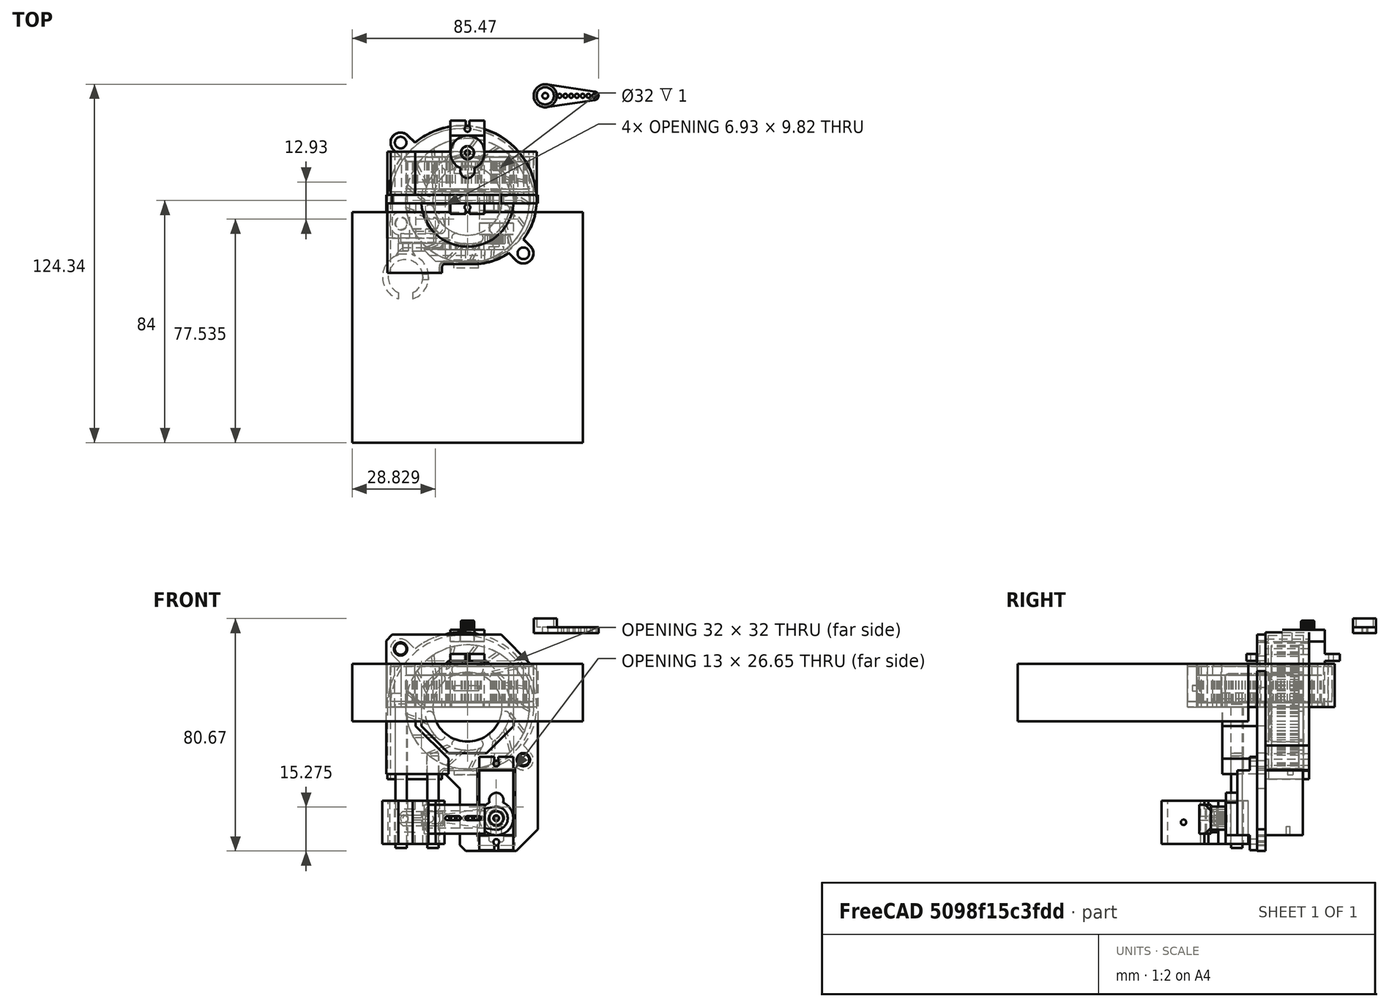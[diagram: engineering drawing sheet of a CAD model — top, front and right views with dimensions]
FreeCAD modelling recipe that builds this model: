
FCSTD DOCUMENT  (FreeCAD 0.17R13522 (Git))
Label: plotter_pen12mm
License: All rights reserved
LicenseURL: http://en.wikipedia.org/wiki/All_rights_reserved
objects: Part::Box×15, Part::Cylinder×15, App::DocumentObjectGroup×11, Part::Cut×11, PartDesign::ShapeBinder×7, Part::Fuse×7, Sketcher::SketchObject×7, Part::MultiFuse×7, Part::Feature×6, Part::Chamfer×6, PartDesign::Point×5, Part::Part2DObjectPython×4, PartDesign::Pocket×4, Mesh::Feature×3, PartDesign::Pad×3, Part::Fillet×2, PartDesign::Body×2, Part::Compound×1, Spreadsheet::Sheet×1, Part::FeaturePython×1, +1 more types
note: 111 computed .brp shape members not serialized (recipe doc carries the construction recipe); baked Part::Feature solids carry a one-line shape summary decoded from their .brp

FEATURE [Part::Feature] Part__Feature  label="TFD-B5015 TITAN"
  Placement = pos=(0,0,7.5) rot=(0,0,1;0rad)
  shape: bbox 51.8 x 51.1 x 15 mm, 65 faces (baked)
FEATURE [Part::Feature] Part__Feature001  label="TFD-B5015 TITAN001"
  shape: bbox 43 x 43 x 11.5 mm, 91 faces (baked)
FEATURE [Part::Part2DObjectPython] Line  # Draft 2D object (typed FeaturePython)
  ChamferSize = 0
  Closed = false
  End = (0,0,10.5)
  FilletRadius = 0
  MakeFace = false
  MapMode = 5
  Points = (2) [(-2.07596,14.8557,11),(0,0,10.5)]
  Start = (-2.07596,14.8557,11)
  Support = -> [Part__Feature001]
FEATURE [Part::Part2DObjectPython] Line001  # Draft 2D object (typed FeaturePython)
  ChamferSize = 0
  Closed = false
  End = (4.6539,11.0608,10.5)
  FilletRadius = 0
  MakeFace = false
  MapMode = 5
  Points = (2) [(0,0,10.5),(4.6539,11.0608,10.5)]
  Start = (0,0,10.5)
  Support = -> [Part__Feature001]
FEATURE [Part::Fillet] Fillet
  Edges = 1 edges r=1: [Edge57]
FEATURE [App::DocumentObjectGroup] Group  label="Inner-part-src"
  Group = -> [Fillet]
FEATURE [Part::Feature] Fillet001  label="Inner-part-final"
  shape: bbox 43 x 43 x 11.5 mm, 153 faces (baked)
FEATURE [Part::Part2DObjectPython] Line002  # Draft 2D object (typed FeaturePython)
  ChamferSize = 0
  Closed = false
  End = (19.4,-18.3,15)
  FilletRadius = 0
  MakeFace = false
  MapMode = 5
  Points = (2) [(0,0,15),(19.4,-18.3,15)]
  Start = (0,0,15)
  Support = -> [Part__Feature]
FEATURE [Part::Part2DObjectPython] Line003  # Draft 2D object (typed FeaturePython)
  ChamferSize = 0
  Closed = false
  End = (-23.2,20.1,15)
  FilletRadius = 0
  MakeFace = false
  MapMode = 5
  Points = (2) [(0,0,15),(-23.2,20.1,15)]
  Start = (0,0,15)
  Support = -> [Part__Feature]
FEATURE [App::DocumentObjectGroup] Construction
  Group = -> [Line,Line001,Line002,Line003]
FEATURE [Part::Cut] Cut  label="cover-1"
  Refine = true
FEATURE [App::DocumentObjectGroup] Group001  label="cover-src"
  Group = -> [Cut]
FEATURE [Part::Feature] Pad005001  label="cover-final"
  Placement = pos=(0,0,-2) rot=(0,0,1;0rad)
  shape: bbox 51.8 x 51 x 15 mm, 33 faces (baked)
FEATURE [Part::Compound] Compound  label="Blower-50x50-final"
  Links = -> [Fillet001,Pad005001]
  Placement = pos=(0,15,0) rot=(1,0,0;1.5708rad)
FEATURE [App::DocumentObjectGroup] Group002  label="Blower"
  Group = -> [Part__Feature,Part__Feature001,Construction,Group,Group001,Compound]
FEATURE [Mesh::Feature] original
FEATURE [Part::Box] Box  label="Cubo"
  AttacherType = Attacher::AttachEngine3D
  Height = 20
  Length = 80
  Placement = pos=(-40,-84,-5) rot=(0,0,1;0rad)
  Width = 80
FEATURE [Mesh::Feature] difference
FEATURE [Mesh::Feature] union
  Placement = pos=(-23,50.7,-49.11) rot=(0,0,1;3.14159rad)
FEATURE [App::DocumentObjectGroup] Group003  label="Fan duct"
  Group = -> [original,Box,difference,union]
FEATURE [PartDesign::ShapeBinder] CopyCompound
  Placement = pos=(0,2,0) rot=(1,0,0;1.5708rad)
FEATURE [PartDesign::Point] DatumPoint  label="DatumPoint_MainScrew1"
  AttacherType = Attacher::AttachEnginePoint
  MapMode = 36
  Placement = pos=(-23.2,2,20.1) rot=(1,0,0;3.14159rad)
  Support = -> [CopyCompound]
FEATURE [PartDesign::ShapeBinder] CopyCompound001
  Placement = pos=(0,2,0) rot=(1,0,0;1.5708rad)
FEATURE [PartDesign::Point] DatumPoint001  label="DatumPoint_MainScrew2"
  AttacherType = Attacher::AttachEnginePoint
  MapMode = 36
  Placement = pos=(19.4,2,-18.3) rot=(1,0,0;3.14159rad)
  Support = -> [CopyCompound001]
FEATURE [Spreadsheet::Sheet] Spreadsheet
  cells = A2=Fan hole diameter; B2(fanHoleDiam)=32; A3=Fan support thickness; B3(FanSuppThick)=3; A4=Fan support width; B4(FanSuppWidth)=10; A5=Shaft thickness; B5(shaftThick)=4; A6=Left Shaft length; B6(shaftLength)=50; A7=Right shaft length; B7(shaftLengthRight)=33; A9=Shaft Axis X position; B9(AxisX)==-Spreadsheet.FanSuppWidth - 13; A10=Shaft Axis Y position; B10(AxisY)=-8; A12=Shaft Axis tolerance; B12(AxisTolerance)=0.20000000000000001; A13=Shaft Axis separation; B13(AxisSeparation)=11; A15=Servo Connecting Rod Flexible Part Thickness; B15(FlexThickness)=0.80000000000000004; A18=Agrandar el prisionero de M2 a M3; A19=Tornillos soporte principal M3; A20=Modificar parte flexible al doble de tamaño
FEATURE [Part::Box] Box001  label="Cubo001"
  AttacherType = Attacher::AttachEngine3D
  Height = 22.7
  Length = 11.8
  Width = 22.5
FEATURE [Part::Box] Box002  label="Cubo002"
  AttacherType = Attacher::AttachEngine3D
  Height = 2.5
  Length = 11.8
  Placement = pos=(0,-4.7,15.9) rot=(0,0,1;0rad)
  Width = 32.4
FEATURE [Part::Fuse] Fusion  label="Square_body"
  Base = -> Box001
  Refine = true
  Tool = -> Box002
FEATURE [Part::Cylinder] Cylinder  label="Cilindro"
  Angle = 360
  AttacherType = Attacher::AttachEngine3D
  Height = 4
  Placement = pos=(5.9,16.6,22.7) rot=(0,0,1;0rad)
  Radius = 5.9
FEATURE [Part::Cylinder] Cylinder001  label="Cilindro001"
  Angle = 360
  AttacherType = Attacher::AttachEngine3D
  Height = 4
  Placement = pos=(5.9,10.3,22.7) rot=(0,0,1;0rad)
  Radius = 2.5
FEATURE [Part::Fuse] Fusion001
  Base = -> Cylinder
  Refine = true
  Tool = -> Cylinder001
FEATURE [Part::Fuse] Fusion003
  Base = -> Fusion
  Refine = true
  Tool = -> Fusion001
FEATURE [Part::Cylinder] Cylinder003  label="Taladro"
  Angle = 360
  AttacherType = Attacher::AttachEngine3D
  Height = 10
  Placement = pos=(5.9,-2.35,11) rot=(0,0,1;0rad)
  Radius = 1
FEATURE [Part::Cylinder] Cylinder004  label="Taladro2"
  Angle = 360
  AttacherType = Attacher::AttachEngine3D
  Height = 10
  Placement = pos=(5.9,24.85,11) rot=(0,0,1;0rad)
  Radius = 1
FEATURE [Part::Fuse] Fusion004  label="Taladros"
  Base = -> Cylinder003
  Refine = true
  Tool = -> Cylinder004
FEATURE [Part::Box] Box003  label="Cubo003"
  AttacherType = Attacher::AttachEngine3D
  Height = 10
  Length = 1.3
  Placement = pos=(5.25,-6,12) rot=(0,0,1;0rad)
  Width = 3.3
FEATURE [Part::Box] Box004  label="Cubo004"
  AttacherType = Attacher::AttachEngine3D
  Height = 10
  Length = 1.3
  Placement = pos=(5.25,25,12) rot=(0,0,1;0rad)
  Width = 3.3
FEATURE [Part::Fuse] Fusion005  label="Rebajes"
  Base = -> Box003
  Refine = true
  Tool = -> Box004
FEATURE [Part::Fuse] Fusion006  label="Taladros001"
  Base = -> Fusion004
  Refine = true
  Tool = -> Fusion005
FEATURE [Part::Cut] Cut001  label="Cuerpo_con_taladros"
  Base = -> Fusion003
  Placement = pos=(-5.9,0,0) rot=(0,0,1;0rad)
  Refine = true
  Tool = -> Fusion006
FEATURE [Part::Cylinder] Cylinder006  label="Cilindro002"
  Angle = 360
  AttacherType = Attacher::AttachEngine3D
  Height = 3
  Placement = pos=(2.51021,16.5511,26.9) rot=(0,0,1;0rad)
  Radius = 0.35
FEATURE [Part::FeaturePython] Array  # Draft array (typed FeaturePython)
  Angle = 360
  ArrayType = 1
  Axis = (0,0,1)
  Base = -> Cylinder006
  Center = (0,16.6,0)
  Fuse = false
  IntervalAxis = (0,0,0)
  IntervalX = (1,0,0)
  IntervalY = (0,1,0)
  IntervalZ = (0,0,0)
  NumberPolar = 20
  NumberX = 2
  NumberY = 2
  NumberZ = 1
FEATURE [Part::Cylinder] Cylinder002  label="Cilindro_interior"
  Angle = 360
  AttacherType = Attacher::AttachEngine3D
  Height = 3.2
  Placement = pos=(0,16.6,26.7) rot=(0,0,1;0rad)
  Radius = 2.3
FEATURE [Part::Cylinder] Cylinder005  label="Cilindro_exterior"
  Angle = 360
  AttacherType = Attacher::AttachEngine3D
  Height = 3.2
  Placement = pos=(0,16.6,26.7) rot=(0,0,1;0rad)
  Radius = 0.85
FEATURE [Part::Cut] Cut002  label="Cilindro_vaciado"
  Base = -> Cylinder002
  Refine = true
  Tool = -> Cylinder005
FEATURE [Part::Fillet] Fillet002
  Base = -> Cut002
  Edges = 1 edges r=0.3: [Edge1]
FEATURE [Part::Cut] Cut003  label="Eje_engranaje"
  Base = -> Fillet002
  Refine = true
  Tool = -> Array
FEATURE [Part::Feature] Fusion007001  label="Servo-sg90-final"
  Placement = pos=(10,14.9,-22) rot=(0,0.707107,-0.707107;3.14159rad)
  shape: bbox 11.8 x 29.9 x 32.4 mm, 77 faces (baked)
  expr: Placement.Base.y = 17.899999999999999 - Spreadsheet.FanSuppThick
FEATURE [App::DocumentObjectGroup] Grupo003  label="Servo"
  Group = -> [Cut001,Cut003,Fusion007001]
FEATURE [Part::Fuse] Fusion008
  Placement = pos=(26.9697,36.3362,25.6722) rot=(0,0,1;0rad)
  Refine = true
FEATURE [App::DocumentObjectGroup] Grupo001  label="1-arm-horn"
  Group = -> [Fusion008]
FEATURE [Part::Feature] Pocket002001  label="Final-1-arm-horn"
  Placement = pos=(9.96971,-16.96,-38.6278) rot=(0,0.707107,0.707107;3.14159rad)
  shape: bbox 22.5 x 5 x 8 mm, 19 faces (baked)
  expr: Placement.Base.y = -13.960000000000001 - Spreadsheet.FanSuppThick
FEATURE [App::DocumentObjectGroup] Group004  label="ServoArm"
  Group = -> [Grupo001,Pocket002001]
FEATURE [PartDesign::ShapeBinder] CopyFusion007001
FEATURE [PartDesign::Point] DatumPoint002  label="DatumPoint_ServoHeight"
  AttacherType = Attacher::AttachEnginePoint
  MapMode = 37
  Placement = pos=(15.9,-8.8,-22) rot=(0,0,1;0rad)
  Support = -> [CopyFusion007001]
FEATURE [PartDesign::ShapeBinder] CopyFusion007001001
  Placement = pos=(15.9,13.9,-22) rot=(0,0.707107,-0.707107;3.14159rad)
FEATURE [PartDesign::Point] DatumPoint003  label="DatumPoint_ServoScrew1"
  AttacherType = Attacher::AttachEnginePoint
  MapMode = 36
  Placement = pos=(10,-4.5,-19.65) rot=(0,0,1;3.14159rad)
  Support = -> [CopyFusion007001001]
FEATURE [PartDesign::ShapeBinder] CopyFusion007001002
  Placement = pos=(15.9,13.9,-22) rot=(0,0.707107,-0.707107;3.14159rad)
FEATURE [PartDesign::Point] DatumPoint004  label="DatumPoint_ServoScrew2"
  AttacherType = Attacher::AttachEnginePoint
  MapMode = 36
  Placement = pos=(10,-4.5,-46.85) rot=(0.908295,0,-0.41833;3.14159rad)
  Support = -> [CopyFusion007001002]
FEATURE [Sketcher::SketchObject] Sketch  label="Sketch_SupportBase"
  ExternalGeometry = -> [DatumPoint,DatumPoint001,DatumPoint002,DatumPoint003,DatumPoint004]
  MapMode = 5
  Placement = pos=(0,0,0) rot=(1,0,0;1.5708rad)
  Support = -> [XZ_Plane]
  expr: Constraints[3] = 0.5 * Spreadsheet.FanSuppWidth
  expr: Constraints[34] = Spreadsheet.fanHoleDiam * 0.5
  expr: Constraints[4] = 0.5 * Spreadsheet.FanSuppWidth
  expr: Constraints[71] = 0.5 * Spreadsheet.FanSuppWidth
  expr: Constraints[72] = 0.5 * Spreadsheet.FanSuppWidth
  sketch-geometry (29):
    g0: LineSegment StartX=-26.0787 StartY=25.1 StartZ=0 EndX=11.6721 EndY=25.1 EndZ=0
    g1: LineSegment StartX=24.4 StartY=12.3721 StartZ=0 EndX=24.4 EndY=-23.3 EndZ=0
    g2: LineSegment StartX=-28.2 StartY=-23.3 StartZ=0 EndX=-28.2 EndY=22.9787 EndZ=0
    g3: Circle CenterX=-23.2 CenterY=20.1 CenterZ=0 NormalX=0 NormalY=0 NormalZ=1 AngleXU=0 Radius=2.3
    g4: Circle CenterX=19.4 CenterY=-18.3 CenterZ=0 NormalX=0 NormalY=0 NormalZ=1 AngleXU=0 Radius=2.3
    g5: LineSegment StartX=16 StartY=6.62742 StartZ=0 EndX=6.62742 EndY=16 EndZ=0
    g6: LineSegment StartX=6.62742 StartY=16 StartZ=0 EndX=-6.62742 EndY=16 EndZ=0
    g7: LineSegment StartX=-6.62742 StartY=16 StartZ=0 EndX=-16 EndY=6.62742 EndZ=0
    g8: LineSegment StartX=-16 StartY=6.62742 StartZ=0 EndX=-16 EndY=-6.62742 EndZ=0
    g9: LineSegment StartX=-16 StartY=-6.62742 StartZ=0 EndX=-6.62742 EndY=-16 EndZ=0
    g10: LineSegment StartX=-6.62742 StartY=-16 StartZ=0 EndX=6.62742 EndY=-16 EndZ=0
    g11: LineSegment StartX=6.62742 StartY=-16 StartZ=0 EndX=16 EndY=-6.62742 EndZ=0
    g12: LineSegment StartX=16 StartY=-6.62742 StartZ=0 EndX=16 EndY=6.62742 EndZ=0
    g13: Circle [constr] CenterX=0 CenterY=0 CenterZ=0 NormalX=0 NormalY=0 NormalZ=1 AngleXU=0 Radius=17.3183
    g14: LineSegment StartX=16.9 StartY=-50 StartZ=0 EndX=-0.551549 EndY=-50 EndZ=0
    g15: LineSegment StartX=-7.74282 StartY=-23.3 StartZ=0 EndX=-28.2 EndY=-23.3 EndZ=0
    g16: Circle CenterX=10.0164 CenterY=-19.6473 CenterZ=0 NormalX=0 NormalY=0 NormalZ=1 AngleXU=0 Radius=1
    g17: LineSegment StartX=16.9 StartY=-50 StartZ=0 EndX=24.4 EndY=-42.5 EndZ=0
    g18: LineSegment StartX=24.4 StartY=-23.3 StartZ=0 EndX=24.4 EndY=-42.5 EndZ=0
    g19: LineSegment StartX=-2.67287 StartY=-28.37 StartZ=0 EndX=-2.67287 EndY=-47.8787 EndZ=0
    g20: LineSegment StartX=-2.67287 StartY=-47.8787 StartZ=0 EndX=-0.551549 EndY=-50 EndZ=0
    g21: LineSegment StartX=3.5 StartY=-21.4 StartZ=0 EndX=16.5 EndY=-21.4 EndZ=0
    g22: LineSegment StartX=16.5 StartY=-21.4 StartZ=0 EndX=16.5 EndY=-45 EndZ=0
    g23: LineSegment StartX=16.5 StartY=-45 StartZ=0 EndX=3.5 EndY=-45 EndZ=0
    g24: LineSegment StartX=3.5 StartY=-45 StartZ=0 EndX=3.5 EndY=-21.4 EndZ=0
    g25: Circle CenterX=10 CenterY=-46.85 CenterZ=0 NormalX=0 NormalY=0 NormalZ=1 AngleXU=0 Radius=1.2
    g26: LineSegment StartX=11.6721 StartY=25.1 StartZ=0 EndX=24.4 EndY=12.3721 EndZ=0
    g27: LineSegment StartX=-26.0787 StartY=25.1 StartZ=0 EndX=-28.2 EndY=22.9787 EndZ=0
    g28: LineSegment StartX=-2.67287 StartY=-28.37 StartZ=0 EndX=-7.74282 EndY=-23.3 EndZ=0
  constraints (75):
    c: Horizontal(g0)
    c: Vertical(g1)
    c: Vertical(g2)
    c: DistanceY(g1,g-4) = 5
    c: DistanceX(g-4,g1) = 5
    c: Coincident(g3,g-3)
    c: Radius(g3) = 2.3
    c: Coincident(g4,g-4)
    c: Radius(g4) = 2.3
    c: Coincident(g5,g6)
    c: Coincident(g6,g7)
    c: Coincident(g7,g8)
    c: Coincident(g8,g9)
    c: Coincident(g9,g10)
    c: Coincident(g10,g11)
    c: Coincident(g11,g12)
    c: Coincident(g12,g5)
    c: Equal(g5, g6-g12) x7
    c: PointOnObject(g5,g13)
    c: PointOnObject(g6,g13)
    c: PointOnObject(g7,g13)
    c: PointOnObject(g8,g13)
    c: PointOnObject(g9,g13)
    c: PointOnObject(g10,g13)
    c: PointOnObject(g11,g13)
    c: PointOnObject(g12,g13)
    c: Coincident(g13,g-1)
    c: Horizontal(g6)
    c: DistanceY(g-1,g5) = 16
    c: DistanceY(g-5,g14) = -28
    c: Horizontal(g14)
    c: DistanceX(g-5,g14) = 1
    c: Coincident(g15,g2)
    c: Radius(g16) = 1.2
    c: Block(g16)
    c: Coincident(g17,g14)
    c: Coincident(g18,g17)
    c: Vertical(g18)
    c: Angle(g18,g17) = 2.35619
    c: Vertical(g19)
    c: Coincident(g19,g20)
    c: Coincident(g20,g14)
    c: Angle(g20,g19) = 2.35619
    c: Coincident(g21,g22)
    c: Coincident(g22,g23)
    c: Coincident(g23,g24)
    c: Coincident(g24,g21)
    c: Horizontal(g21)
    c: Horizontal(g23)
    c: Vertical(g22)
    c: Vertical(g24)
    c: DistanceX(g-5,g21) = 0.6
    c: DistanceY(g-5,g21) = 0.6
    c: DistanceX(g23,g21) = 13
    c: DistanceY(g23,g21) = 23.6
    c: Horizontal(g15)
    c: PointOnObject(g1,g15)
    c: Coincident(g25,g-7)
    c: Radius(g25) = 1.2
    c: Coincident(g0,g26)
    c: Coincident(g26,g1)
    c: Angle(g0,g26) = 2.35619
    c: Distance(g26) = 18
    c: Coincident(g2,g27)
    c: Coincident(g0,g27)
    c: DistanceX(g2,g3) = 5
    c: DistanceY(g3,g0) = 5
    c: Distance(g27) = 3
    c: Angle(g27,g0) = 2.35619
    c: Coincident(g18,g1)
    c: Distance(g20) = 3
    c: Coincident(g15,g28)
    c: Coincident(g28,g19)
    c: Angle(g15,g28) = 2.35619
    c: Distance(g28) = 7.17
FEATURE [PartDesign::Pad] Pad
  Length = 3
  Length2 = 100
  Placement = pos=(0,0,0) rot=(1,0,0;1.5708rad)
  Profile = -> Sketch
  Type = 0
  expr: Length = Spreadsheet.FanSuppThick
FEATURE [Sketcher::SketchObject] Sketch001  label="Sketch_AxisSupport"
  ExternalGeometry = -> [Pad]
  MapMode = 5
  Placement = pos=(0,-3,0) rot=(1,0,0;1.5708rad)
  Support = -> [Pad]
  sketch-geometry (8):
    g0: LineSegment StartX=-26.0787 StartY=4.82132 StartZ=0 EndX=-20.1213 EndY=4.82132 EndZ=0
    g1: LineSegment StartX=-18 StartY=2.7 StartZ=0 EndX=-20.1213 EndY=4.82132 EndZ=0
    g2: LineSegment StartX=-26.0787 StartY=4.82132 StartZ=0 EndX=-28.2 EndY=2.7 EndZ=0
    g3: LineSegment StartX=-18 StartY=2.7 StartZ=0 EndX=-18 EndY=-6.62742 EndZ=0
    g4: LineSegment StartX=-18 StartY=-6.62742 StartZ=0 EndX=-6.62742 EndY=-18 EndZ=0
    g5: LineSegment StartX=-6.62742 StartY=-18 StartZ=0 EndX=-6.62742 EndY=-23.3 EndZ=0
    g6: LineSegment StartX=-6.62742 StartY=-23.3 StartZ=0 EndX=-28.2 EndY=-23.3 EndZ=0
    g7: LineSegment StartX=-28.2 StartY=-23.3 StartZ=0 EndX=-28.2 EndY=2.7 EndZ=0
  constraints (23):
    c: Horizontal(g0)
    c: Coincident(g1,g0)
    c: Coincident(g0,g2)
    c: Angle(g2,g0) = 2.35619
    c: Angle(g0,g1) = 2.35619
    c: Equal(g1,g2)
    c: Distance(g1) = 3
    c: Vertical(g3)
    c: Coincident(g3,g4)
    c: Coincident(g4,g5)
    c: Vertical(g5)
    c: Coincident(g5,g6)
    c: Coincident(g6,g-3)
    c: Horizontal(g6)
    c: Coincident(g6,g7)
    c: Vertical(g7)
    c: Coincident(g7,g2)
    c: Coincident(g3,g1)
    c: PointOnObject(g-4,g5)
    c: DistanceY(g4,g-4) = 2
    c: DistanceX(g3,g-4) = 2
    c: Angle(g4,g3) = 2.35619
    c: DistanceY(g6,g2) = 26
FEATURE [Part::Cylinder] Cylinder007  label="ShaftLeft"
  Angle = 360
  AttacherType = Attacher::AttachEngine3D
  Height = 50
  Placement = pos=(-23,-8,-49) rot=(0,0,1;0rad)
  Radius = 2
  expr: Placement.Base.y = Spreadsheet.AxisY
  expr: Placement.Base.x = Spreadsheet.AxisX
  expr: Height = Spreadsheet.shaftLength
  expr: Radius = Spreadsheet.shaftThick * 0.5
FEATURE [PartDesign::Pad] Pad005002
  BaseFeature = -> Pad
  Length = 12
  Length2 = 100
  Placement = pos=(0,0,0) rot=(1,0,0;1.5708rad)
  Profile = -> Sketch001
  Type = 0
FEATURE [Part::Cylinder] Cylinder008  label="ShaftRight"
  Angle = 360
  AttacherType = Attacher::AttachEngine3D
  Height = 33
  Placement = pos=(-12,-8,-49) rot=(0,0,1;0rad)
  Radius = 2
  expr: Placement.Base.y = Spreadsheet.AxisY
  expr: Placement.Base.x = Spreadsheet.AxisX + Spreadsheet.AxisSeparation
  expr: Height = Spreadsheet.shaftLengthRight
  expr: Radius = Spreadsheet.shaftThick * 0.5
FEATURE [Sketcher::SketchObject] Sketch002  label="Sketch_AxisLeftHole"
  AttachmentOffset = pos=(24,0,-28.2) rot=(0,1,0;1.5708rad)
  MapMode = 5
  Placement = pos=(0,2e-12,-24) rot=(1,0,0;3.14159rad)
  Support = -> [Pad005002]
  expr: Constraints[4] = 2.1499999999999999
  expr: Constraints[3] = Spreadsheet.AxisSeparation
  expr: Constraints[1] = -Spreadsheet.AxisY + 2
  expr: Constraints[0] = -Spreadsheet.AxisX
  sketch-geometry (2):
    g0: Circle CenterX=-23 CenterY=10 CenterZ=0 NormalX=0 NormalY=0 NormalZ=1 AngleXU=0 Radius=2.15
    g1: Circle [constr] CenterX=-12 CenterY=10 CenterZ=0 NormalX=0 NormalY=0 NormalZ=1 AngleXU=0 Radius=2.15
  constraints (6):
    c: DistanceX(g0,g-1) = 23
    c: DistanceY(g-1,g0) = 10
    c: DistanceY(g1,g0) = 0
    c: DistanceX(g0,g1) = 11
    c: Radius(g1) = 2.15
    c: Radius(g0) = 2.15
FEATURE [Sketcher::SketchObject] Sketch003  label="Sketch_AxisRightHole"
  AttachmentOffset = pos=(24,0,-28.2) rot=(0,1,0;1.5708rad)
  MapMode = 5
  Placement = pos=(0,2e-12,-24) rot=(1,0,0;3.14159rad)
  Support = -> [Pad005002]
  expr: Constraints[4] = 2.1499999999999999
  expr: Constraints[3] = Spreadsheet.AxisSeparation
  expr: Constraints[1] = -Spreadsheet.AxisY + 2
  expr: Constraints[0] = -Spreadsheet.AxisX
  sketch-geometry (2):
    g0: Circle [constr] CenterX=-23 CenterY=10 CenterZ=0 NormalX=0 NormalY=0 NormalZ=1 AngleXU=0 Radius=2.15
    g1: Circle CenterX=-12 CenterY=10 CenterZ=0 NormalX=0 NormalY=0 NormalZ=1 AngleXU=0 Radius=2.15
  constraints (6):
    c: DistanceX(g0,g-1) = 23
    c: DistanceY(g-1,g0) = 10
    c: DistanceY(g1,g0) = 0
    c: DistanceX(g0,g1) = 11
    c: Radius(g1) = 2.15
    c: Radius(g0) = 2.15
FEATURE [PartDesign::Pocket] Pocket
  BaseFeature = -> Pad005002
  Length = 24
  Length2 = 100
  Placement = pos=(0,0,0) rot=(1,0,0;1.5708rad)
  Profile = -> Sketch002
  Type = 0
FEATURE [PartDesign::Pocket] Pocket002002
  BaseFeature = -> Pocket
  Length = 7
  Length2 = 100
  Placement = pos=(0,0,0) rot=(1,0,0;1.5708rad)
  Profile = -> Sketch003
  Type = 0
FEATURE [Sketcher::SketchObject] Sketch004  label="Sketch_ServoCableHole"
  ExternalGeometry = -> [Pocket002002]
  MapMode = 5
  Placement = pos=(0,-3,0) rot=(1,0,0;1.5708rad)
  Support = -> [Pocket002002]
  sketch-geometry (7):
    g0: LineSegment StartX=12.5 StartY=-43.35 StartZ=0 EndX=7.5 EndY=-43.35 EndZ=0
    g1: LineSegment StartX=7.5 StartY=-43.35 StartZ=0 EndX=7.5 EndY=-46.35 EndZ=0
    g2: LineSegment StartX=7.5 StartY=-46.35 StartZ=0 EndX=8 EndY=-46.85 EndZ=0
    g3: LineSegment StartX=12 StartY=-46.85 StartZ=0 EndX=12.5 EndY=-46.35 EndZ=0
    g4: LineSegment StartX=12.5 StartY=-46.35 StartZ=0 EndX=12.5 EndY=-43.35 EndZ=0
    g5: LineSegment StartX=8 StartY=-46.85 StartZ=0 EndX=10 EndY=-46.85 EndZ=0
    g6: LineSegment StartX=10 StartY=-46.85 StartZ=0 EndX=12 EndY=-46.85 EndZ=0
  constraints (20):
    c: Horizontal(g0)
    c: Coincident(g0,g1)
    c: Vertical(g1)
    c: Coincident(g1,g2)
    c: Coincident(g3,g4)
    c: Coincident(g4,g0)
    c: Vertical(g4)
    c: Equal(g2,g3)
    c: Coincident(g5,g2)
    c: Coincident(g5,g-3)
    c: Horizontal(g5)
    c: Coincident(g6,g5)
    c: Coincident(g6,g3)
    c: Equal(g6,g5)
    c: Horizontal(g6)
    c: Equal(g4,g1)
    c: DistanceX(g0,g0) = 5
    c: DistanceX(g6,g6) = 2
    c: Angle(g3,g6) = 2.35619
    c: DistanceY(g4,g4) = 3
FEATURE [PartDesign::Pocket] Pocket002003
  BaseFeature = -> Pocket002002
  Length = 5
  Length2 = 100
  Placement = pos=(0,0,0) rot=(1,0,0;1.5708rad)
  Profile = -> Sketch004
  Type = 1
FEATURE [PartDesign::Body] Body  label="Part 1 - MainSupportPart"
  Group = -> [Sketch,DatumPoint,CopyCompound,DatumPoint001,CopyCompound001,DatumPoint002,CopyFusion007001,DatumPoint003,CopyFusion007001001,DatumPoint004,CopyFusion007001002,Pad,Sketch001,Pad005002,Sketch002,Sketch003,Pocket,Pocket002002,Sketch004,Pocket002003]
  Origin = -> Origin
  Placement = pos=(0,2,0) rot=(0,0,1;0rad)
  Tip = -> Pocket002003
FEATURE [PartDesign::ShapeBinder] CopyBox005
  Placement = pos=(-11,-11,-47.5) rot=(0,0,1;3.14159rad)
FEATURE [Sketcher::SketchObject] Sketch005  label="SketchShaftTubes"
  ExternalGeometry = -> [CopyBox005]
  MapMode = 5
  Placement = pos=(-11,-11,-47.5) rot=(0,1,0;3.14159rad)
  Support = -> [CopyBox005]
  expr: Constraints[17] = 2 + Spreadsheet.AxisTolerance
  sketch-geometry (8):
    g0: LineSegment [constr] StartX=0 StartY=0 StartZ=0 EndX=6.5 EndY=0 EndZ=0
    g1: LineSegment [constr] StartX=6.5 StartY=0 StartZ=0 EndX=13 EndY=0 EndZ=0
    g2: ArcOfCircle CenterX=1 CenterY=3 CenterZ=0 NormalX=0 NormalY=0 NormalZ=1 AngleXU=0 Radius=4 StartAngle=1.5708 EndAngle=4.71239
    g3: ArcOfCircle CenterX=12 CenterY=3 CenterZ=0 NormalX=0 NormalY=0 NormalZ=1 AngleXU=0 Radius=4 StartAngle=4.71239 EndAngle=7.85398
    g4: LineSegment StartX=1 StartY=-1 StartZ=0 EndX=12 EndY=-1 EndZ=0
    g5: LineSegment StartX=1 StartY=7 StartZ=0 EndX=12 EndY=7 EndZ=0
    g6: Circle CenterX=1 CenterY=3 CenterZ=0 NormalX=0 NormalY=0 NormalZ=1 AngleXU=0 Radius=2.2
    g7: Circle CenterX=12 CenterY=3 CenterZ=0 NormalX=0 NormalY=0 NormalZ=1 AngleXU=0 Radius=2.2
  constraints (19):
    c: Coincident(g0,g-1)
    c: Coincident(g1,g0)
    c: Coincident(g1,g-3)
    c: Equal(g0,g1)
    c: Horizontal(g0)
    c: Tangent(g2,g5) = 1.5708
    c: Tangent(g2,g4) = -1.5708
    c: Tangent(g4,g3) = -1.5708
    c: Tangent(g5,g3) = 1.5708
    c: Horizontal(g4)
    c: Equal(g2,g3)
    c: DistanceX(g2,g0) = 5.5
    c: DistanceX(g0,g3) = 5.5
    c: DistanceY(g0,g2) = 3
    c: Radius(g2) = 4
    c: Coincident(g6,g2)
    c: Coincident(g7,g3)
    c: Radius(g7) = 2.2
    c: Equal(g6,g7)
FEATURE [PartDesign::ShapeBinder] CopyBox005001
  Placement = pos=(-11,-11,-47.5) rot=(0,0,1;3.14159rad)
FEATURE [Part::Box] Box005  label="Cube"
  AttacherType = Attacher::AttachEngine3D
  Height = 15
  Length = 13
  Placement = pos=(-11,-11,-47.5) rot=(0,0,1;3.14159rad)
  Width = 3.5
FEATURE [App::DocumentObjectGroup] Group005  label="Printer Parts"
  Group = -> [Group002,Group003,Grupo003,Group004]
FEATURE [Part::Box] Box006  label="Cube001"
  AttacherType = Attacher::AttachEngine3D
  Height = 4
  Length = 5
  Placement = pos=(-24,-23,-47.5) rot=(0,0,1;0rad)
  Width = 11
FEATURE [Part::Box] Box007  label="Cube002"
  AttacherType = Attacher::AttachEngine3D
  Height = 18
  Length = 5
  Placement = pos=(-24,-38,-49) rot=(0,0,1;0rad)
  Width = 11
FEATURE [Part::Cylinder] Cylinder009  label="Cylinder"
  Angle = 360
  AttacherType = Attacher::AttachEngine3D
  Height = 19
  Placement = pos=(-21.5,-26.5,-49.5) rot=(0,0,1;0rad)
  Radius = 6
FEATURE [Part::Cylinder] Cylinder010  label="Cylinder001"
  Angle = 360
  AttacherType = Attacher::AttachEngine3D
  Height = 15
  Placement = pos=(-21.5,-26.5,-47.5) rot=(0,0,1;0rad)
  Radius = 8
FEATURE [Part::Box] Box008  label="Cube003"
  AttacherType = Attacher::AttachEngine3D
  Height = 8
  Length = 5
  Placement = pos=(-24,-23.5,-43.5) rot=(0,0,1;0rad)
  Width = 5
FEATURE [Part::Box] Box009  label="Cube004"
  AttacherType = Attacher::AttachEngine3D
  Height = 3
  Length = 5
  Placement = pos=(-24,-23,-35.5) rot=(0,0,1;0rad)
  Width = 11
FEATURE [Part::Cylinder] Cylinder011  label="Cylinder002"
  Angle = 360
  AttacherType = Attacher::AttachEngine3D
  Height = 10
  Placement = pos=(-12.5,-26.5,-40) rot=(0,-1,0;1.5708rad)
  Radius = 0.95
FEATURE [Part::Box] Box010  label="Cube005"
  AttacherType = Attacher::AttachEngine3D
  Height = 5
  Length = 15.5
  Placement = pos=(-24,-17.5,-41.25) rot=(0,0,1;0rad)
  Width = 2.7
FEATURE [Part::Box] Box011  label="Cube006"
  AttacherType = Attacher::AttachEngine3D
  Height = 10
  Length = 21
  Placement = pos=(-15,-21,-44) rot=(0,0,1;0rad)
  Width = 4
FEATURE [Part::Cylinder] Cylinder012  label="Cylinder003"
  Angle = 360
  AttacherType = Attacher::AttachEngine3D
  Height = 10
  Placement = pos=(-3,-14.5,-38.6) rot=(1,0,0;1.5708rad)
  Radius = 0.7
FEATURE [Part::Box] Box012  label="Cube007"
  AttacherType = Attacher::AttachEngine3D
  Height = 1.4
  Length = 4
  Placement = pos=(-7,-24.5,-39.3) rot=(0,0,1;0rad)
  Width = 10
FEATURE [Part::Cylinder] Cylinder013  label="Cylinder004"
  Angle = 360
  AttacherType = Attacher::AttachEngine3D
  Height = 10
  Placement = pos=(-7,-14.5,-38.6) rot=(1,0,0;1.5708rad)
  Radius = 0.7
FEATURE [Part::MultiFuse] Fusion007005
  Placement = pos=(7,0,0) rot=(0,0,1;0rad)
  Refine = true
  Shapes = -> [Cylinder013,Box012,Cylinder012]
FEATURE [Part::MultiFuse] Fusion007006
  Refine = true
  Shapes = -> [Cylinder013,Box012,Cylinder012]
FEATURE [Part::Cut] Cut007
  Base = -> Box011
  Refine = true
  Tool = -> Fusion007006
FEATURE [Part::Cut] Cut008
  Base = -> Cut007
  Refine = true
  Tool = -> Fusion007005
FEATURE [Part::Cylinder] Cylinder014  label="Cylinder005"
  Angle = 360
  AttacherType = Attacher::AttachEngine3D
  Height = 5
  Placement = pos=(-21.5,-13.5,-38.75) rot=(1,0,0;1.5708rad)
  Radius = 1
FEATURE [Part::Cut] Cut009
  Base = -> Box010
  Refine = true
  Tool = -> Cylinder014
FEATURE [Part::Chamfer] Chamfer001
  Base = -> Cut009
  Edges = 2 edges r=1.5: [Edge2,Edge4]
FEATURE [Part::Chamfer] Chamfer002
  Base = -> Chamfer001
  Edges = 2 edges r=1.2: [Edge5,Edge8]
FEATURE [Part::Chamfer] Chamfer003
  Base = -> Cut008
  Edges = 1 edges r=3.8: [Edge1]
FEATURE [Part::MultiFuse] Fusion007007
  Refine = true
  Shapes = -> [Chamfer002,Chamfer003]
FEATURE [Part::Chamfer] Chamfer005  label="ConnectingRod_Without flexible part"
  Base = -> Fusion007007
  Edges = 2 edges r=2: [Edge41,Edge44]
FEATURE [Part::Chamfer] Chamfer004
  Base = -> Fusion007007
  Edges = 2 edges r=0.9: [Edge14,Edge27]
FEATURE [Part::Box] Box013  label="Cube008"
  AttacherType = Attacher::AttachEngine3D
  Height = 2.85
  Length = 3
  Placement = pos=(-19,-19,-42) rot=(0,0,1;0rad)
  Width = 10
  expr: Height = 3.25 - 0.5 * Spreadsheet.FlexThickness
FEATURE [Part::Box] Box014  label="Cube009"
  AttacherType = Attacher::AttachEngine3D
  Height = 3.25
  Length = 3
  Placement = pos=(-19,-19,-38.35) rot=(0,0,1;0rad)
  Width = 10
  expr: Placement.Base.z = -38.75 + 0.5 * Spreadsheet.FlexThickness
  expr: Height = 3.25
FEATURE [Part::MultiFuse] Fusion007008
  Refine = true
  Shapes = -> [Box014,Box013]
FEATURE [Part::Cut] Cut010  label="Final_ConnectingRod"
  Base = -> Chamfer005
  Refine = true
  Tool = -> Fusion007008
FEATURE [App::DocumentObjectGroup] Group007  label="Part 3 - Connecting Rod"
  Group = -> [Chamfer004,Cut010]
FEATURE [PartDesign::Body] Body001  label="SupportPen"
  BaseFeature = -> Fusion007002
  Group = -> [BaseFeature,CopyBox005,Sketch005,Pocket002004,Pad005003,CopyBox005001,Sketch006]
  Origin = -> Origin001
  Tip = -> Pocket002004
FEATURE [PartDesign::Pad] Pad005003
  BaseFeature = -> Pocket002004
  Length = 15
  Length2 = 100
  Profile = -> Sketch005
  Reversed = true
  Type = 0
FEATURE [Part::MultiFuse] Fusion007002
  Refine = true
  Shapes = -> [Pad005003,Box005]
FEATURE [Sketcher::SketchObject] Sketch006  label="Sketch_Groove"
  MapMode = 5
  Placement = pos=(0,0,-47.5) rot=(1,0,0;3.14159rad)
  Support = -> [Fusion007002]
  sketch-geometry (4):
    g0: ArcOfCircle CenterX=-22 CenterY=-38.75 CenterZ=0 NormalX=0 NormalY=0 NormalZ=1 AngleXU=0 Radius=1.25 StartAngle=1.5708 EndAngle=4.71239
    g1: ArcOfCircle CenterX=-13 CenterY=-38.75 CenterZ=0 NormalX=0 NormalY=0 NormalZ=1 AngleXU=0 Radius=1.25 StartAngle=4.71239 EndAngle=7.85398
    g2: LineSegment StartX=-22 StartY=-40 StartZ=0 EndX=-13 EndY=-40 EndZ=0
    g3: LineSegment StartX=-22 StartY=-37.5 StartZ=0 EndX=-13 EndY=-37.5 EndZ=0
  constraints (10):
    c: Tangent(g0,g3) = 1.5708
    c: Tangent(g0,g2) = -1.5708
    c: Tangent(g2,g1) = -1.5708
    c: Tangent(g3,g1) = 1.5708
    c: Horizontal(g2)
    c: Equal(g0,g1)
    c: Radius(g1) = 1.25
    c: DistanceX(g3,g3) = 9
    c: DistanceX(g1,g-1) = 13
    c: DistanceY(g1,g-1) = 37.5
FEATURE [PartDesign::FeatureBase] BaseFeature
  BaseFeature = -> Fusion007002
FEATURE [PartDesign::Pocket] Pocket002004  label="Support1"
  BaseFeature = -> BaseFeature
  Length = 3
  Length2 = 3
  Profile = -> Sketch006
  Type = 0
FEATURE [App::DocumentObjectGroup] Group006  label="Part 2 - Pen Support Example 1"
  Group = -> [Body001,Fusion007002,Cut006]
FEATURE [Part::MultiFuse] Fusion007003
  Refine = true
  Shapes = -> [Pocket002004,Box009,Box006,Cylinder010]
FEATURE [Part::Chamfer] Chamfer
  Base = -> Fusion007003
  Edges = 4 edges r=1: [Edge27,Edge34,Edge45,Edge48]
FEATURE [Part::MultiFuse] Fusion007004
  Refine = true
  Shapes = -> [Box008,Chamfer]
FEATURE [Part::Cut] Cut004
  Base = -> Fusion007004
  Refine = true
  Tool = -> Cylinder009
FEATURE [Part::Cut] Cut005
  Base = -> Cut004
  Refine = true
  Tool = -> Box007
FEATURE [Part::Cut] Cut006  label="Final_PenSupport1"
  Base = -> Cut005
  Refine = true
  Tool = -> Cylinder011
